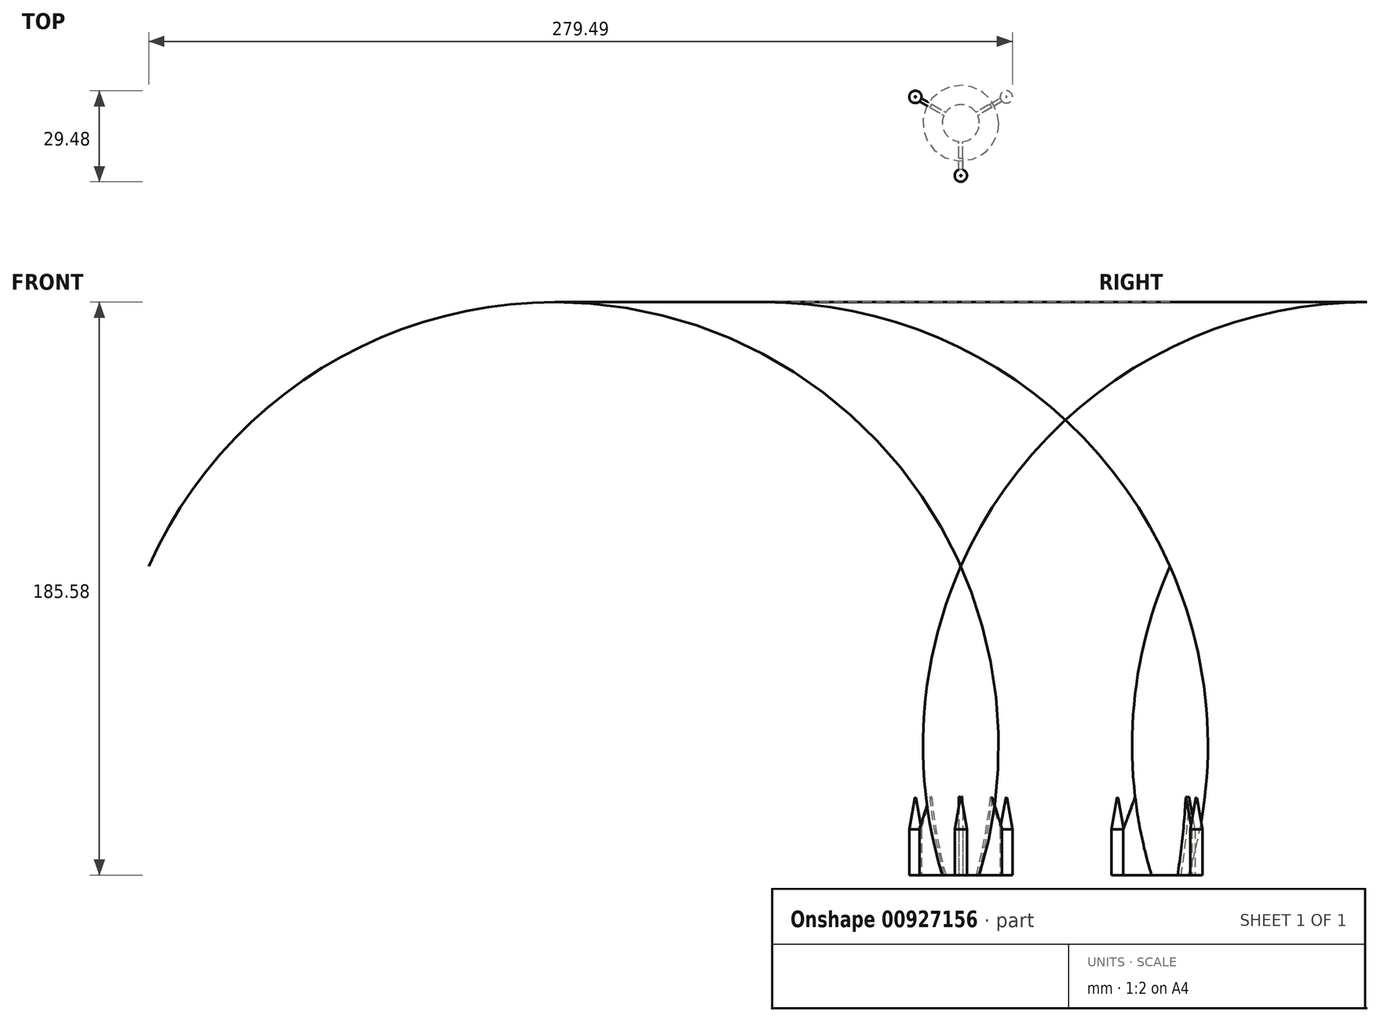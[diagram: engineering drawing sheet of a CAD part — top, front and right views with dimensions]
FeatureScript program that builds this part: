
annotation { "Feature Type Name" : "Feature", "Feature Type Description" : "" }
export const myFeature = defineFeature(function(context is Context, id is Id, definition is map)
    precondition{}
    {
        {
            var Q0;
            Q0=qCreatedBy(makeId("Front.planeOp"),FACE);
            var sketch = newSketch(context, id + "F0", { "sketchPlane" : qUnion([Q0])});
            skLineSegment(sketch, "E0", {"start": v(6, 0) * mm, "end": v(0, 0) * mm});
            skLineSegment(sketch, "E1", {"start": v(0, 0) * mm, "end": v(0, 100) * mm});
            skArc(sketch, "E2", {"start": v(6, 0) * mm, "mid": v(12, 50.54) * mm, "end": v(0, 100) * mm});
            skLineSegment(sketch, "E3", {"start": v(0, 9.4) * mm, "end": v(12, 9.4) * mm, "construction": true});
            skPoint(sketch, "E3.endSnap0", {"position": v(12, 50.54) * mm});
            skSolve(sketch);
        }
        {
            var Q0;
            Q0=makeQuery(id+"F0.imprint","IMPRINT",FACE,{"disambiguationData":[TD([[makeQuery(id+"F0.imprint","IMPRINT",EDGE,{"derivedFrom":sQuery(id+"F0.wireOp",EDGE,"E0")}),-1.0]])]});
            var Q1;
            Q1=sQuery(id+"F0.wireOp",EDGE,"E1");
            revolve(context, id + "F1", {"surfaceOperationType" : NewSurfaceOperationType.NEW, "entities" : qUnion([Q0]), "axis" : qUnion([Q1]), "revolveType" : RevolveType.FULL});
        }
        {
            var Q0;
            Q0=qCreatedBy(makeId("Top.planeOp"),FACE);
            var sketch = newSketch(context, id + "F2", { "sketchPlane" : qUnion([Q0])});
            skCircle(sketch, "E4", {"center": v(0, -17) * mm, "radius": 1.99 * mm});
            skLineSegment(sketch, "E5.bottom", {"start": v(0.6, -17) * mm, "end": v(-0.6, -17) * mm});
            skLineSegment(sketch, "E5.top", {"start": v(0.6, 0) * mm, "end": v(-0.6, 0) * mm});
            skLineSegment(sketch, "E5.left", {"start": v(0.6, -17) * mm, "end": v(0.6, 0) * mm});
            skLineSegment(sketch, "E5.right", {"start": v(-0.6, -17) * mm, "end": v(-0.6, 0) * mm});
            skLineSegment(sketch, "E6.bottom", {"start": v(0, -17) * mm, "end": v(0, -17) * mm});
            skLineSegment(sketch, "E6.top", {"start": v(0, -17) * mm, "end": v(0, -17) * mm});
            skLineSegment(sketch, "E6.left", {"start": v(0, -17) * mm, "end": v(0, -17) * mm});
            skLineSegment(sketch, "E6.right", {"start": v(0, -17) * mm, "end": v(0, -17) * mm});
            skCircle(sketch, "E7.1.0", {"center": v(14.72, 8.5) * mm, "radius": 1.99 * mm});
            skLineSegment(sketch, "E7.1.1", {"start": v(14.42, 9.02) * mm, "end": v(-0.3, 0.52) * mm});
            skLineSegment(sketch, "E7.1.2", {"start": v(15.02, 7.98) * mm, "end": v(0.3, -0.52) * mm});
            skCircle(sketch, "E7.2.0", {"center": v(-14.72, 8.5) * mm, "radius": 1.99 * mm});
            skLineSegment(sketch, "E7.2.1", {"start": v(-15.02, 7.98) * mm, "end": v(-0.3, -0.52) * mm});
            skLineSegment(sketch, "E7.2.2", {"start": v(-14.42, 9.02) * mm, "end": v(0.3, 0.52) * mm});
            skPoint(sketch, "E7.center", {"position": v(0, 0) * mm});
            skSolve(sketch);
        }
        {
            var Q0;
            {var subQ6=sQuery(id+"F2.wireOp",EDGE,"E5.top");Q0=makeQuery(id+"F2.imprint","IMPRINT",FACE,{"disambiguationData":[TD([[makeQuery(id+"F2.imprint","IMPRINT",EDGE,{"derivedFrom":subQ6}),-1.0]])]});}
            var Q1;
            {var subQ1=sQuery(id+"F2.wireOp",EDGE,"E5.top");Q1=makeQuery(id+"F2.imprint","IMPRINT",FACE,{"disambiguationData":[TD([[makeQuery(id+"F2.imprint","IMPRINT",EDGE,{"derivedFrom":subQ1}),1.0]])]});}
            extrude(context, id + "F3", {"entities" : qUnion([Q0, Q1]), "operationType" : NewBodyOperationType.ADD, "depth" : 35 * mm, "offsetDistance" : 25 * mm});
        }
        {
            var Q0;
            Q0=makeQuery(id+"F3.opExtrude","CAP_EDGE",EDGE,{"disambiguationData":[OSD([sQuery(id+"F2.wireOp",EDGE,"E7.2.0")])],"isStart":false});
            var Q1;
            Q1=makeQuery(id+"F3.opExtrude","CAP_EDGE",EDGE,{"disambiguationData":[OSD([sQuery(id+"F2.wireOp",EDGE,"E4")])],"isStart":false});
            var Q2;
            Q2=makeQuery(id+"F3.opExtrude","CAP_EDGE",EDGE,{"disambiguationData":[OSD([sQuery(id+"F2.wireOp",EDGE,"E7.1.0")])],"isStart":false});
            chamfer(context, id + "F4", {"entities" : qUnion([Q0, Q1, Q2]), "chamferType" : ChamferType.OFFSET_ANGLE, "width" : 20 * mm, "oppositeDirection" : false, "angle" : 20 * degree, "tangentPropagation" : true});
        }
        {
            var Q0;
            {var subQ5=sQuery(id+"F2.wireOp",EDGE,"E5.bottom");Q0=makeQuery(id+"F2.imprint","IMPRINT",FACE,{"disambiguationData":[TD([[makeQuery(id+"F2.imprint","IMPRINT",EDGE,{"derivedFrom":subQ5}),-1.0]])]});}
            var Q1;
            {var subQ5=sQuery(id+"F2.wireOp",EDGE,"E5.bottom");Q1=makeQuery(id+"F2.imprint","IMPRINT",FACE,{"disambiguationData":[TD([[makeQuery(id+"F2.imprint","IMPRINT",EDGE,{"derivedFrom":subQ5}),1.0]])]});}
            var Q2;
            {var subQ0=sQuery(id+"F2.wireOp",EDGE,"E7.1.0");var subQ1=makeQuery(id+"F2.imprint","INTERSECT",VERTEX,{"derivedFrom":[subQ0,sQuery(id+"F2.wireOp",EDGE,"E7.1.1")]});Q2=makeQuery(id+"F2.imprint","IMPRINT",FACE,{"disambiguationData":[TD([[makeQuery(id+"F2.imprint","IMPRINT",EDGE,{"disambiguationData":[TD([[subQ1,-1.0]])],"derivedFrom":subQ0}),1.0]])]});}
            var Q3;
            {var subQ0=sQuery(id+"F2.wireOp",EDGE,"E7.2.0");var subQ1=makeQuery(id+"F2.imprint","INTERSECT",VERTEX,{"derivedFrom":[subQ0,sQuery(id+"F2.wireOp",EDGE,"E7.2.1")]});Q3=makeQuery(id+"F2.imprint","IMPRINT",FACE,{"disambiguationData":[TD([[makeQuery(id+"F2.imprint","IMPRINT",EDGE,{"disambiguationData":[TD([[subQ1,-1.0]])],"derivedFrom":subQ0}),1.0]])]});}
            extrude(context, id + "F5", {"entities" : qUnion([Q0, Q1, Q2, Q3]), "operationType" : NewBodyOperationType.ADD, "depth" : 20 * mm, "offsetDistance" : 25 * mm});
        }
        {
            var Q0;
            Q0=makeQuery(id+"F5.opExtrude","CAP_FACE",FACE,{"disambiguationData":[OSD([sQuery(id+"F2.wireOp",EDGE,"E4")])],"isStart":false});
            var Q1;
            Q1=makeQuery(id+"F5.opExtrude","CAP_FACE",FACE,{"disambiguationData":[OSD([sQuery(id+"F2.wireOp",EDGE,"E7.2.0")])],"isStart":false});
            var Q2;
            Q2=makeQuery(id+"F5.opExtrude","CAP_FACE",FACE,{"disambiguationData":[OSD([sQuery(id+"F2.wireOp",EDGE,"E7.1.0")])],"isStart":false});
            extrude(context, id + "F6", {"entities" : qUnion([Q0, Q1, Q2]), "operationType" : NewBodyOperationType.ADD, "depth" : 5 * mm, "offsetDistance" : 25 * mm});
        }
        {
            var Q0;
            Q0=makeQuery(id+"F6.opExtrude","CAP_EDGE",EDGE,{"disambiguationData":[OSD([sQuery(id+"F2.wireOp",EDGE,"E7.2.0")])],"isStart":false});
            var Q1;
            Q1=makeQuery(id+"F6.opExtrude","CAP_EDGE",EDGE,{"disambiguationData":[OSD([sQuery(id+"F2.wireOp",EDGE,"E4")])],"isStart":false});
            var Q2;
            Q2=makeQuery(id+"F6.opExtrude","CAP_EDGE",EDGE,{"disambiguationData":[OSD([sQuery(id+"F2.wireOp",EDGE,"E7.1.0")])],"isStart":false});
            chamfer(context, id + "F7", {"entities" : qUnion([Q0, Q1, Q2]), "chamferType" : ChamferType.OFFSET_ANGLE, "width" : 1.8 * mm, "oppositeDirection" : false, "angle" : 80 * degree, "tangentPropagation" : true});
        }
    });
